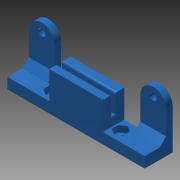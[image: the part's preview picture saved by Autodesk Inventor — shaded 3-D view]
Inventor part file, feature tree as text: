
AUTODESK INVENTOR PART (.ipt)
format: ipt  version: 2013 SP2 (Build 170200200, 200)  size: 187,904 bytes
history: native  units: mm
features: extrude x7, sketch x5, fillet x2, chamfer x1
ambient origin geometry x8: Origin, YZ Plane, XZ Plane, XY Plane, X Axis, Y Axis, Z Axis, Center Point
bodies: Solid1 (feature_tree)
feature tree (15):
  sketch  "Sketch1"  dims[d0=40.0mm d1=10.0mm]
  extrude  "Extrusion1"  Depth=10.0mm
  extrude  "Extrusion5"  Depth=25.0mm
  sketch  "Sketch2"  dims[d4=5.0mm d5=0.0mm d14=25.0mm]
  extrude  "Extrusion2"  Depth=13.0mm TaperAngle=0.0deg
  fillet  "Fillet1"  Radius=3.2mm
  extrude  "Extrusion3"  Depth=4.0mm
  extrude  "Extrusion4"  Depth=2.0mm
  extrude  "Extrusion7"  Depth=4.0mm
  extrude  "Extrusion6"  Depth=4.0mm
  chamfer  "Chamfer2"  Distance=1.0mm
  fillet  "Fillet2"  Radius=3.0mm
  sketch  "Sketch3"  dims[d15=25.0mm d20=13.0mm d21=0.0mm d22=3.2mm]
  sketch  "Sketch4"  dims[d23=3.2mm d24=4.0mm]
  sketch  "Sketch5"  dims[d25=4.0mm d31=2.0mm d32=4.0mm d33=4.0mm d34=1.0mm d37=3.0mm d38=0.0mm d39=5.5mm d40=5.5mm d41=4.0mm d42=0.0mm d43=12.0mm d44=12.0mm d45=13.0mm d46=13.0mm d47=5.0mm d48=0.0mm d49=3.2mm d50=3.2mm d52=5.0mm d53=0.0mm d54=20.0mm d55=0.0mm d56=4.0mm d57=3.0mm d58=2.0mm d59=45.0deg d60=6.0mm]
